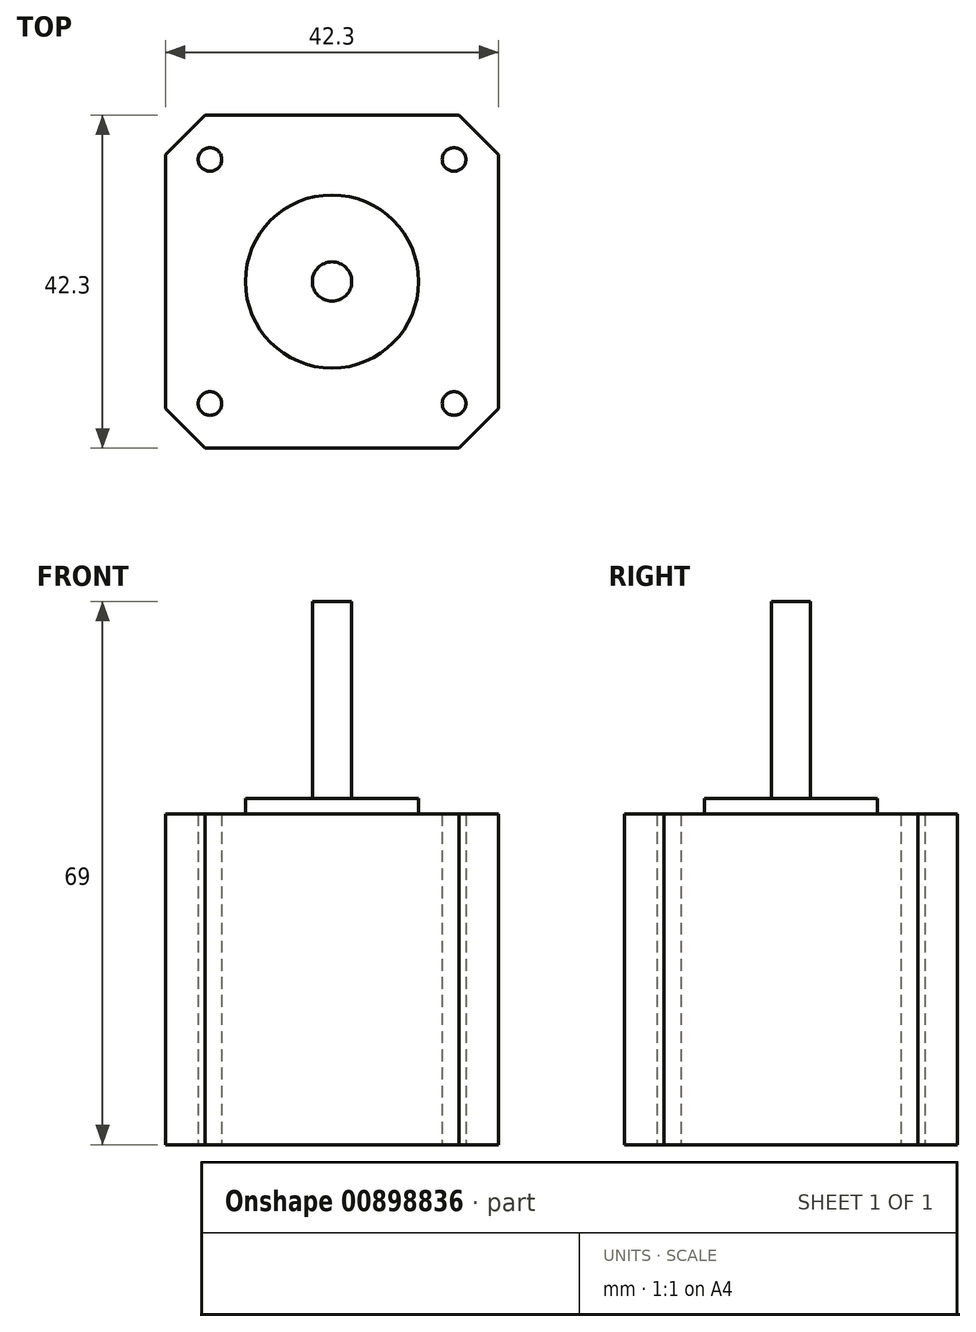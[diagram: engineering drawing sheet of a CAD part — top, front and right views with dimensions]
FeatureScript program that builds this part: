
annotation { "Feature Type Name" : "Feature", "Feature Type Description" : "" }
export const myFeature = defineFeature(function(context is Context, id is Id, definition is map)
    precondition{}
    {
        {
            var Q0;
            Q0=qCreatedBy(makeId("Top.planeOp"),FACE);
            var sketch = newSketch(context, id + "F0", { "sketchPlane" : qUnion([Q0])});
            skLineSegment(sketch, "E0.bottom", {"start": v(-21.15, -21.15) * mm, "end": v(21.15, -21.15) * mm});
            skLineSegment(sketch, "E0.top", {"start": v(-21.15, 21.15) * mm, "end": v(21.15, 21.15) * mm});
            skLineSegment(sketch, "E0.left", {"start": v(-21.15, -21.15) * mm, "end": v(-21.15, 21.15) * mm});
            skLineSegment(sketch, "E0.right", {"start": v(21.15, -21.15) * mm, "end": v(21.15, 21.15) * mm});
            skPoint(sketch, "E0.middle", {"position": v(0, 0) * mm});
            skLineSegment(sketch, "E1.bottom", {"start": v(-15.5, -15.5) * mm, "end": v(15.5, -15.5) * mm, "construction": true});
            skLineSegment(sketch, "E1.top", {"start": v(-15.5, 15.5) * mm, "end": v(15.5, 15.5) * mm, "construction": true});
            skLineSegment(sketch, "E1.left", {"start": v(-15.5, -15.5) * mm, "end": v(-15.5, 15.5) * mm, "construction": true});
            skLineSegment(sketch, "E1.right", {"start": v(15.5, -15.5) * mm, "end": v(15.5, 15.5) * mm, "construction": true});
            skCircle(sketch, "E2", {"center": v(-15.5, 15.5) * mm, "radius": 1.5 * mm});
            skCircle(sketch, "E3", {"center": v(15.5, 15.5) * mm, "radius": 1.5 * mm});
            skCircle(sketch, "E4", {"center": v(15.5, -15.5) * mm, "radius": 1.5 * mm});
            skCircle(sketch, "E5", {"center": v(-15.5, -15.5) * mm, "radius": 1.5 * mm});
            skSolve(sketch);
        }
        {
            var Q0;
            Q0=makeQuery(id+"F0.imprint","IMPRINT",FACE,{"disambiguationData":[TD([[makeQuery(id+"F0.imprint","IMPRINT",EDGE,{"derivedFrom":sQuery(id+"F0.wireOp",EDGE,"E0.bottom")}),1.0]])]});
            var Q1;
            Q1=sQuery(id+"F0.wireOp",EDGE,"E0.top");
            var Q2;
            Q2=sQuery(id+"F0.wireOp",EDGE,"E0.left");
            var Q3;
            Q3=sQuery(id+"F0.wireOp",EDGE,"E0.bottom");
            var Q4;
            Q4=sQuery(id+"F0.wireOp",EDGE,"E0.right");
            extrude(context, id + "F1", {"entities" : qUnion([Q0]), "surfaceEntities" : qUnion([Q1, Q2, Q3, Q4]), "depth" : 42 * mm, "offsetDistance" : 25 * mm});
        }
        {
            var Q0;
            Q0=makeQuery(id+"F1.opExtrude","CAP_FACE",FACE,{"disambiguationData":[OSD([sQuery(id+"F0.wireOp",EDGE,"E0.bottom"),sQuery(id+"F0.wireOp",EDGE,"E0.top"),sQuery(id+"F0.wireOp",EDGE,"E0.left"),sQuery(id+"F0.wireOp",EDGE,"E0.right"),sQuery(id+"F0.wireOp",EDGE,"E2"),sQuery(id+"F0.wireOp",EDGE,"E3"),sQuery(id+"F0.wireOp",EDGE,"E4"),sQuery(id+"F0.wireOp",EDGE,"E5")])],"isStart":false});
            var sketch = newSketch(context, id + "F2", { "sketchPlane" : qUnion([Q0])});
            skCircle(sketch, "E6", {"center": v(0, 0) * mm, "radius": 11 * mm});
            skSolve(sketch);
        }
        {
            var Q0;
            Q0=makeQuery(id+"F2.imprint","IMPRINT",FACE,{"disambiguationData":[TD([[makeQuery(id+"F2.imprint","IMPRINT",EDGE,{"derivedFrom":sQuery(id+"F2.wireOp",EDGE,"E6")}),1.0]])]});
            extrude(context, id + "F3", {"entities" : qUnion([Q0]), "operationType" : NewBodyOperationType.ADD, "depth" : 2 * mm, "offsetDistance" : 25 * mm});
        }
        {
            var Q0;
            Q0=makeQuery(id+"F3.opExtrude","CAP_FACE",FACE,{"disambiguationData":[OSD([sQuery(id+"F2.wireOp",EDGE,"E6")])],"isStart":false});
            var sketch = newSketch(context, id + "F4", { "sketchPlane" : qUnion([Q0])});
            skCircle(sketch, "E7", {"center": v(0, 0) * mm, "radius": 2.5 * mm});
            skSolve(sketch);
        }
        {
            var Q0;
            Q0=makeQuery(id+"F4.imprint","IMPRINT",FACE,{"disambiguationData":[TD([[makeQuery(id+"F4.imprint","IMPRINT",EDGE,{"derivedFrom":sQuery(id+"F4.wireOp",EDGE,"E7")}),1.0]])]});
            extrude(context, id + "F5", {"entities" : qUnion([Q0]), "operationType" : NewBodyOperationType.ADD, "depth" : 25 * mm, "offsetDistance" : 25 * mm});
        }
        {
            var Q0;
            Q0=makeQuery(id+"F1.opExtrude","SWEPT_EDGE",EDGE,{"disambiguationData":[OSD([sQuery(id+"F0.wireOp",EDGE,"E0.bottom"),sQuery(id+"F0.wireOp",EDGE,"E0.left")])]});
            var Q1;
            Q1=makeQuery(id+"F1.opExtrude","SWEPT_EDGE",EDGE,{"disambiguationData":[OSD([sQuery(id+"F0.wireOp",EDGE,"E0.bottom"),sQuery(id+"F0.wireOp",EDGE,"E0.right")])]});
            var Q2;
            Q2=makeQuery(id+"F1.opExtrude","SWEPT_EDGE",EDGE,{"disambiguationData":[OSD([sQuery(id+"F0.wireOp",EDGE,"E0.top"),sQuery(id+"F0.wireOp",EDGE,"E0.right")])]});
            var Q3;
            Q3=makeQuery(id+"F1.opExtrude","SWEPT_EDGE",EDGE,{"disambiguationData":[OSD([sQuery(id+"F0.wireOp",EDGE,"E0.top"),sQuery(id+"F0.wireOp",EDGE,"E0.left")])]});
            chamfer(context, id + "F6", {"entities" : qUnion([Q0, Q1, Q2, Q3]), "width" : 5 * mm});
        }
    });
